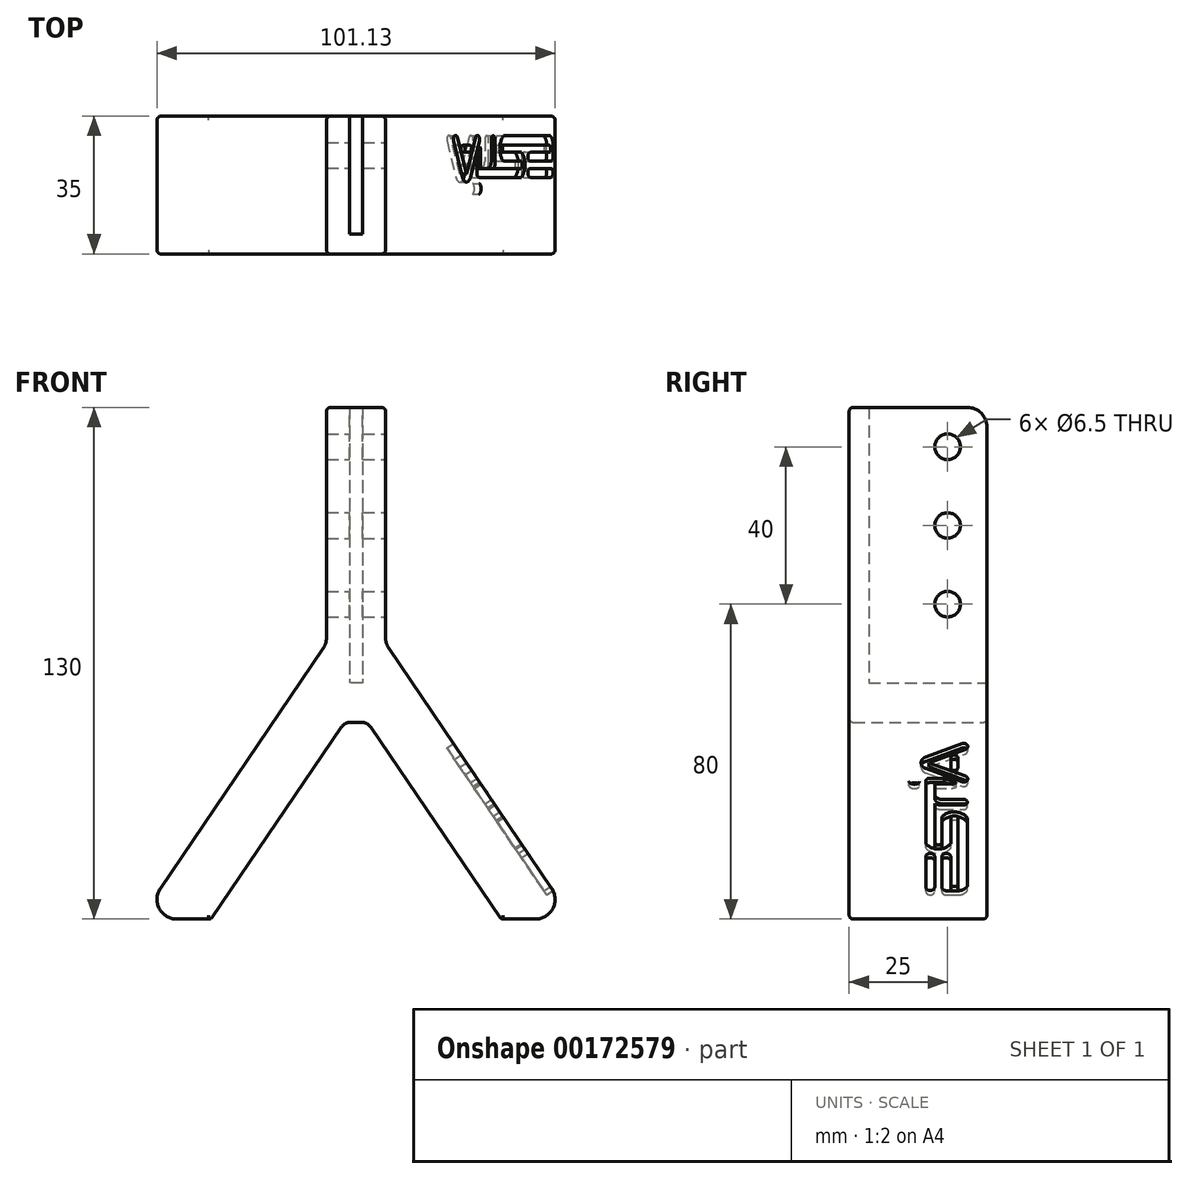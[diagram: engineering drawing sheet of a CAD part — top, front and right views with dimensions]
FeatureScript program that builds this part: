
annotation { "Feature Type Name" : "Feature", "Feature Type Description" : "" }
export const myFeature = defineFeature(function(context is Context, id is Id, definition is map)
    precondition{}
    {
        {
            var Q0;
            Q0=qCreatedBy(makeId("Front.planeOp"),FACE);
            var sketch = newSketch(context, id + "F0", { "sketchPlane" : qUnion([Q0])});
            skLineSegment(sketch, "E0", {"start": v(0, 0) * mm, "end": v(137.14, 0) * mm});
            skLineSegment(sketch, "E1", {"start": v(137.14, 0) * mm, "end": v(68.57, 101.05) * mm});
            skPoint(sketch, "E1.endSnap0", {"position": v(68.57, 0) * mm});
            skLineSegment(sketch, "E2", {"start": v(68.57, 101.05) * mm, "end": v(0, 0) * mm});
            skLineSegment(sketch, "E3.bottom", {"start": v(61.07, 90) * mm, "end": v(76.07, 90) * mm});
            skLineSegment(sketch, "E3.top", {"start": v(61.07, 150) * mm, "end": v(76.07, 150) * mm});
            skLineSegment(sketch, "E3.left", {"start": v(61.07, 90) * mm, "end": v(61.07, 150) * mm});
            skLineSegment(sketch, "E3.right", {"start": v(76.07, 90) * mm, "end": v(76.07, 150) * mm});
            skLineSegment(sketch, "E4.bottom", {"start": v(13.57, 0) * mm, "end": v(123.57, 0) * mm});
            skLineSegment(sketch, "E4.top", {"start": v(13.57, 20) * mm, "end": v(123.57, 20) * mm});
            skLineSegment(sketch, "E4.left", {"start": v(13.57, 0) * mm, "end": v(13.57, 20) * mm});
            skLineSegment(sketch, "E4.right", {"start": v(123.57, 0) * mm, "end": v(123.57, 20) * mm});
            skSolve(sketch);
        }
        {
            var Q0;
            Q0=makeQuery(id+"F0.imprint","IMPRINT",FACE,{"disambiguationData":[TD([[makeQuery(id+"F0.imprint","IMPRINT",EDGE,{"derivedFrom":sQuery(id+"F0.wireOp",EDGE,"E4.bottom")}),1.0]])]});
            var Q1;
            {var subQ0=sQuery(id+"F0.wireOp",EDGE,"E3.bottom");Q1=makeQuery(id+"F0.imprint","IMPRINT",FACE,{"disambiguationData":[TD([[makeQuery(id+"F0.imprint","IMPRINT",EDGE,{"derivedFrom":subQ0}),-1.0]])]});}
            var Q2;
            {var subQ3=sQuery(id+"F0.wireOp",EDGE,"E3.bottom");Q2=makeQuery(id+"F0.imprint","IMPRINT",FACE,{"disambiguationData":[TD([[makeQuery(id+"F0.imprint","IMPRINT",EDGE,{"derivedFrom":subQ3}),1.0]])]});}
            var Q3;
            Q3=makeQuery(id+"F0.imprint","IMPRINT",FACE,{"disambiguationData":[TD([[makeQuery(id+"F0.imprint","IMPRINT",EDGE,{"derivedFrom":sQuery(id+"F0.wireOp",EDGE,"E3.top")}),-1.0]])]});
            extrude(context, id + "F1", {"entities" : qUnion([Q0, Q1, Q2, Q3]), "depth" : 35 * mm, "offsetDistance" : 25 * mm});
        }
        {
            var Q0;
            Q0=makeQuery(id+"F1.opExtrude","CAP_FACE",FACE,{"disambiguationData":[OSD([sQuery(id+"F0.wireOp",EDGE,"E0"),sQuery(id+"F0.wireOp",EDGE,"E1"),sQuery(id+"F0.wireOp",EDGE,"E2"),sQuery(id+"F0.wireOp",EDGE,"E3.top"),sQuery(id+"F0.wireOp",EDGE,"E3.left"),sQuery(id+"F0.wireOp",EDGE,"E3.right")])],"isStart":true});
            var sketch = newSketch(context, id + "F2", { "sketchPlane" : qUnion([Q0])});
            skLineSegment(sketch, "E5.bottom", {"start": v(-70.27, 150) * mm, "end": v(-66.87, 150) * mm});
            skLineSegment(sketch, "E5.top", {"start": v(-70.27, 80) * mm, "end": v(-66.87, 80) * mm});
            skLineSegment(sketch, "E5.left", {"start": v(-70.27, 150) * mm, "end": v(-70.27, 80) * mm});
            skLineSegment(sketch, "E5.right", {"start": v(-66.87, 150) * mm, "end": v(-66.87, 80) * mm});
            skSolve(sketch);
        }
        {
            var Q0;
            Q0 = qSketchRegion(id + "F2", true);
            extrude(context, id + "F3", {"entities" : qUnion([Q0]), "operationType" : NewBodyOperationType.REMOVE, "oppositeDirection" : true, "depth" : 30 * mm, "offsetDistance" : 25 * mm});
        }
        {
            var Q0;
            Q0=makeQuery(id+"F1.opExtrude","SWEPT_FACE",FACE,{"disambiguationData":[OSD([sQuery(id+"F0.wireOp",EDGE,"E3.right")])]});
            var sketch = newSketch(context, id + "F4", { "sketchPlane" : qUnion([Q0])});
            skCircle(sketch, "E6", {"center": v(-10, 140) * mm, "radius": 3.25 * mm});
            skCircle(sketch, "E7", {"center": v(-10, 120) * mm, "radius": 3.25 * mm});
            skCircle(sketch, "E8", {"center": v(-10, 100) * mm, "radius": 3.25 * mm});
            skSolve(sketch);
        }
        {
            var Q0;
            Q0 = qSketchRegion(id + "F4", true);
            extrude(context, id + "F5", {"entities" : qUnion([Q0]), "operationType" : NewBodyOperationType.REMOVE, "oppositeDirection" : true, "depth" : 25 * mm, "offsetDistance" : 25 * mm});
        }
        {
            var Q0;
            Q0=makeQuery(id+"F1.opExtrude","CAP_FACE",FACE,{"disambiguationData":[OSD([sQuery(id+"F0.wireOp",EDGE,"E1"),sQuery(id+"F0.wireOp",EDGE,"E2"),sQuery(id+"F0.wireOp",EDGE,"E3.top"),sQuery(id+"F0.wireOp",EDGE,"E3.left"),sQuery(id+"F0.wireOp",EDGE,"E3.right"),sQuery(id+"F0.wireOp",EDGE,"E4.bottom"),sQuery(id+"F0.wireOp",EDGE,"E4.left"),sQuery(id+"F0.wireOp",EDGE,"E4.right")])],"isStart":true});
            var sketch = newSketch(context, id + "F6", { "sketchPlane" : qUnion([Q0])});
            skLineSegment(sketch, "E9", {"start": v(-112.23, 10) * mm, "end": v(-71.52, 70) * mm});
            skLineSegment(sketch, "E10", {"start": v(-71.52, 70) * mm, "end": v(-65.63, 70) * mm});
            skLineSegment(sketch, "E11", {"start": v(-65.63, 70) * mm, "end": v(-24.91, 10) * mm});
            skLineSegment(sketch, "E12", {"start": v(-24.91, 10) * mm, "end": v(-112.23, 10) * mm});
            skSolve(sketch);
        }
        {
            var Q0;
            Q0 = qSketchRegion(id + "F6", true);
            extrude(context, id + "F7", {"entities" : qUnion([Q0]), "operationType" : NewBodyOperationType.REMOVE, "endBound" : BoundingType.THROUGH_ALL, "oppositeDirection" : true, "depth" : 25 * mm, "offsetDistance" : 25 * mm});
        }
        {
            var Q0;
            Q0=makeQuery(id+"F7.boolean.opBoolean","COPY",EDGE,{"derivedFrom":makeQuery(id+"F7.opExtrude","SWEPT_EDGE",EDGE,{"disambiguationData":[OSD([sQuery(id+"F6.wireOp",EDGE,"E11"),sQuery(id+"F6.wireOp",EDGE,"E12")])]})});
            var Q1;
            Q1=makeQuery(id+"F7.boolean.opBoolean","COPY",EDGE,{"derivedFrom":makeQuery(id+"F7.opExtrude","SWEPT_EDGE",EDGE,{"disambiguationData":[OSD([sQuery(id+"F6.wireOp",EDGE,"E9"),sQuery(id+"F6.wireOp",EDGE,"E12")])]})});
            var Q2;
            Q2=makeQuery(id+"F1.opExtrude","SWEPT_EDGE",EDGE,{"disambiguationData":[OSD([sQuery(id+"F0.wireOp",EDGE,"E2"),sQuery(id+"F0.wireOp",EDGE,"E4.top"),sQuery(id+"F0.wireOp",EDGE,"E4.left")])]});
            var Q3;
            Q3=makeQuery(id+"F1.opExtrude","SWEPT_EDGE",EDGE,{"disambiguationData":[OSD([sQuery(id+"F0.wireOp",EDGE,"E1"),sQuery(id+"F0.wireOp",EDGE,"E4.top"),sQuery(id+"F0.wireOp",EDGE,"E4.right")])]});
            var Q4;
            Q4=makeQuery(id+"F1.opExtrude","SWEPT_EDGE",EDGE,{"disambiguationData":[OSD([sQuery(id+"F0.wireOp",EDGE,"E2"),sQuery(id+"F0.wireOp",EDGE,"E3.bottom"),sQuery(id+"F0.wireOp",EDGE,"E3.left")])]});
            var Q5;
            Q5=makeQuery(id+"F1.opExtrude","SWEPT_EDGE",EDGE,{"disambiguationData":[OSD([sQuery(id+"F0.wireOp",EDGE,"E1"),sQuery(id+"F0.wireOp",EDGE,"E3.bottom"),sQuery(id+"F0.wireOp",EDGE,"E3.right")])]});
            fillet(context, id + "F8", {"entities" : qUnion([Q0, Q1, Q2, Q3, Q4, Q5]), "radius" : 5 * mm, "tangentPropagation" : true, "allowEdgeOverflow" : false});
        }
        {
            var Q0;
            Q0=makeQuery(id+"F7.boolean.opBoolean","COPY",EDGE,{"derivedFrom":makeQuery(id+"F7.opExtrude","SWEPT_EDGE",EDGE,{"disambiguationData":[OSD([sQuery(id+"F6.wireOp",EDGE,"E9"),sQuery(id+"F6.wireOp",EDGE,"E10")])]})});
            var Q1;
            Q1=makeQuery(id+"F7.boolean.opBoolean","COPY",EDGE,{"derivedFrom":makeQuery(id+"F7.opExtrude","SWEPT_EDGE",EDGE,{"disambiguationData":[OSD([sQuery(id+"F6.wireOp",EDGE,"E10"),sQuery(id+"F6.wireOp",EDGE,"E11")])]})});
            fillet(context, id + "F9", {"entities" : qUnion([Q0, Q1]), "radius" : 3 * mm, "tangentPropagation" : true, "allowEdgeOverflow" : false});
        }
        {
            var Q0;
            {var subQ0=sQuery(id+"F0.wireOp",EDGE,"E3.right");var subQ1=sQuery(id+"F0.wireOp",EDGE,"E3.top");Q0=makeQuery(id+"F3.boolean.opBoolean","SPLIT",EDGE,{"disambiguationData":[TD([makeQuery(id+"F1.opExtrude","SWEPT_FACE",FACE,{"disambiguationData":[OSD([subQ0])]})])],"derivedFrom":makeQuery(id+"F1.opExtrude","CAP_EDGE",EDGE,{"disambiguationData":[OSD([subQ1])],"isStart":true})});}
            var Q1;
            {var subQ0=sQuery(id+"F0.wireOp",EDGE,"E3.left");var subQ1=sQuery(id+"F0.wireOp",EDGE,"E3.top");Q1=makeQuery(id+"F3.boolean.opBoolean","SPLIT",EDGE,{"disambiguationData":[TD([makeQuery(id+"F1.opExtrude","SWEPT_FACE",FACE,{"disambiguationData":[OSD([subQ0])]})])],"derivedFrom":makeQuery(id+"F1.opExtrude","CAP_EDGE",EDGE,{"disambiguationData":[OSD([subQ1])],"isStart":true})});}
            fillet(context, id + "F10", {"entities" : qUnion([Q0, Q1]), "radius" : 5 * mm, "tangentPropagation" : true, "allowEdgeOverflow" : false});
        }
        {
            var Q0;
            Q0=makeQuery(id+"F1.opExtrude","CAP_EDGE",EDGE,{"disambiguationData":[OSD([sQuery(id+"F0.wireOp",EDGE,"E3.right")])],"isStart":false});
            var Q1;
            Q1=makeQuery(id+"F1.opExtrude","CAP_EDGE",EDGE,{"disambiguationData":[OSD([sQuery(id+"F0.wireOp",EDGE,"E3.left")])],"isStart":false});
            fillet(context, id + "F11", {"entities" : qUnion([Q0, Q1]), "radius" : 1 * mm, "tangentPropagation" : true, "allowEdgeOverflow" : false});
        }
        {
            var Q0;
            Q0=makeQuery(id+"F1.opExtrude","CAP_EDGE",EDGE,{"disambiguationData":[OSD([sQuery(id+"F0.wireOp",EDGE,"E3.top")])],"isStart":false});
            fillet(context, id + "F12", {"entities" : qUnion([Q0]), "radius" : 1 * mm, "tangentPropagation" : true, "allowEdgeOverflow" : false});
        }
        {
            var Q0;
            Q0=makeQuery(id+"F7.boolean.opBoolean","COPY",EDGE,{"derivedFrom":makeQuery(id+"F7.opExtrude","CAP_EDGE",EDGE,{"disambiguationData":[OSD([sQuery(id+"F6.wireOp",EDGE,"E11")])],"isStart":true})});
            var Q1;
            Q1=makeQuery(id+"F7.boolean.opBoolean","INTERSECT",EDGE,{"derivedFrom":[makeQuery(id+"F1.opExtrude","CAP_FACE",FACE,{"disambiguationData":[OSD([sQuery(id+"F0.wireOp",EDGE,"E1"),sQuery(id+"F0.wireOp",EDGE,"E2"),sQuery(id+"F0.wireOp",EDGE,"E3.top"),sQuery(id+"F0.wireOp",EDGE,"E3.left"),sQuery(id+"F0.wireOp",EDGE,"E3.right"),sQuery(id+"F0.wireOp",EDGE,"E4.bottom"),sQuery(id+"F0.wireOp",EDGE,"E4.left"),sQuery(id+"F0.wireOp",EDGE,"E4.right")])],"isStart":false}),makeQuery(id+"F7.opExtrude","SWEPT_FACE",FACE,{"disambiguationData":[OSD([sQuery(id+"F6.wireOp",EDGE,"E11")])]})]});
            fillet(context, id + "F13", {"entities" : qUnion([Q0, Q1]), "radius" : 1 * mm, "tangentPropagation" : true, "allowEdgeOverflow" : false});
        }
        {
            var Q0;
            Q0=makeQuery(id+"F1.opExtrude","SWEPT_FACE",FACE,{"disambiguationData":[OSD([sQuery(id+"F0.wireOp",EDGE,"E1")])]});
            var sketch = newSketch(context, id + "F14", { "sketchPlane" : qUnion([Q0])});
            skLineSegment(sketch, "E13.0.0", {"start": v(-7.78, -42.77) * mm, "end": v(-9.2, -42.77) * mm});
            skLineSegment(sketch, "E13.0.1", {"start": v(-9.2, -42.77) * mm, "end": v(-9.2, -33.77) * mm});
            skLineSegment(sketch, "E13.0.38", {"start": v(-11.48, -33.77) * mm, "end": v(-11.48, -42.9) * mm});
            skLineSegment(sketch, "E13.0.57", {"start": v(-10.28, -44.1) * mm, "end": v(-7.34, -44.1) * mm});
            skArc(sketch, "E13.0.59", {"start": v(-7.34, -44.1) * mm, "mid": v(-6, -43.75) * mm, "end": v(-5, -42.77) * mm});
            skLineSegment(sketch, "E13.0.60", {"start": v(-5, -42.77) * mm, "end": v(-5, -21.7) * mm});
            skArc(sketch, "E13.0.61", {"start": v(-5, -21.7) * mm, "mid": v(-8.2, -19.91) * mm, "end": v(-11.48, -21.55) * mm});
            skLineSegment(sketch, "E13.0.62", {"start": v(-11.48, -21.55) * mm, "end": v(-11.48, -29.73) * mm});
            skArc(sketch, "E13.0.63", {"start": v(-11.48, -29.73) * mm, "mid": v(-12.38, -30.04) * mm, "end": v(-13.27, -29.7) * mm});
            skLineSegment(sketch, "E13.0.64", {"start": v(-13.27, -29.7) * mm, "end": v(-13.27, -17.32) * mm});
            skArc(sketch, "E13.0.65", {"start": v(-13.27, -17.32) * mm, "mid": v(-12.4, -17.7) * mm, "end": v(-11.46, -17.82) * mm});
            skLineSegment(sketch, "E13.0.66", {"start": v(-11.46, -17.82) * mm, "end": v(-5.86, -17.82) * mm});
            skArc(sketch, "E13.0.67", {"start": v(-5.86, -17.82) * mm, "mid": v(-5, -16.96) * mm, "end": v(-5.86, -16.1) * mm});
            skLineSegment(sketch, "E13.0.68", {"start": v(-5.86, -16.1) * mm, "end": v(-11.46, -16.1) * mm});
            skArc(sketch, "E13.0.69", {"start": v(-11.46, -16.1) * mm, "mid": v(-12.74, -15.56) * mm, "end": v(-13.27, -14.28) * mm});
            skLineSegment(sketch, "E13.0.70", {"start": v(-13.27, -14.28) * mm, "end": v(-13.27, -11.3) * mm});
            skLineSegment(sketch, "E13.0.71", {"start": v(-13.27, -11.3) * mm, "end": v(-9, -11.3) * mm});
            skArc(sketch, "E13.0.72", {"start": v(-9, -11.3) * mm, "mid": v(-8.36, -11.2) * mm, "end": v(-7.78, -10.89) * mm});
            skLineSegment(sketch, "E13.0.73", {"start": v(-7.78, -10.89) * mm, "end": v(-10.78, -9.58) * mm});
            skLineSegment(sketch, "E13.0.74", {"start": v(-10.78, -9.58) * mm, "end": v(-14.6, -9.58) * mm});
            skArc(sketch, "E13.0.75", {"start": v(-14.6, -9.58) * mm, "mid": v(-15.28, -9.86) * mm, "end": v(-15.55, -10.53) * mm});
            skLineSegment(sketch, "E13.0.76", {"start": v(-15.55, -10.53) * mm, "end": v(-15.55, -29.67) * mm});
            skArc(sketch, "E13.0.77", {"start": v(-15.55, -29.67) * mm, "mid": v(-12.39, -31.34) * mm, "end": v(-9.2, -29.73) * mm});
            skLineSegment(sketch, "E13.0.78", {"start": v(-9.2, -29.73) * mm, "end": v(-9.2, -21.55) * mm});
            skArc(sketch, "E13.0.79", {"start": v(-9.2, -21.55) * mm, "mid": v(-8.3, -21.12) * mm, "end": v(-7.4, -21.55) * mm});
            skLineSegment(sketch, "E13.0.80", {"start": v(-7.4, -21.55) * mm, "end": v(-7.4, -42.39) * mm});
            skArc(sketch, "E13.0.81", {"start": v(-7.4, -42.39) * mm, "mid": v(-7.5, -42.66) * mm, "end": v(-7.78, -42.77) * mm});
            skLineSegment(sketch, "E14.0.2", {"start": v(-13.27, -42.9) * mm, "end": v(-13.27, -33.77) * mm});
            skLineSegment(sketch, "E14.0.39", {"start": v(-15.55, -33.77) * mm, "end": v(-15.55, -42.9) * mm});
            skLineSegment(sketch, "E15.0.0", {"start": v(-14.77, -4.83) * mm, "end": v(-5.47, -0.77) * mm});
            skArc(sketch, "E15.0.1", {"start": v(-5.47, -0.77) * mm, "mid": v(-4.96, 0.52) * mm, "end": v(-6.25, 1.02) * mm});
            skLineSegment(sketch, "E15.0.2", {"start": v(-6.25, 1.02) * mm, "end": v(-15.55, -3.04) * mm});
            skArc(sketch, "E15.0.3", {"start": v(-15.55, -3.04) * mm, "mid": v(-16.72, -4.83) * mm, "end": v(-15.55, -6.62) * mm});
            skLineSegment(sketch, "E15.0.4", {"start": v(-15.55, -6.62) * mm, "end": v(-6.25, -10.69) * mm});
            skArc(sketch, "E15.0.5", {"start": v(-6.25, -10.69) * mm, "mid": v(-4.96, -10.18) * mm, "end": v(-5.47, -8.9) * mm});
            skLineSegment(sketch, "E15.0.6", {"start": v(-5.47, -8.9) * mm, "end": v(-14.77, -4.83) * mm});
            skLineSegment(sketch, "E16.0.2", {"start": v(-7.4, -6.33) * mm, "end": v(-7.4, -3.33) * mm});
            skLineSegment(sketch, "E16.0.39", {"start": v(-9.2, -3.33) * mm, "end": v(-9.2, -6.33) * mm});
            skLineSegment(sketch, "E17", {"start": v(-5.86, -16.96) * mm, "end": v(-5.86, 0.13) * mm, "construction": true});
            skLineSegment(sketch, "E18", {"start": v(-8.3, -22.26) * mm, "end": v(-8.3, -43.3) * mm, "construction": true});
            skLineSegment(sketch, "E19", {"start": v(-12.35, -47.78) * mm, "end": v(-12.35, -28.66) * mm, "construction": true});
            skArc(sketch, "E20", {"start": v(-15.55, -42.9) * mm, "mid": v(-14.41, -44.05) * mm, "end": v(-13.27, -42.9) * mm});
            skArc(sketch, "E21", {"start": v(-13.27, -33.77) * mm, "mid": v(-14.41, -32.63) * mm, "end": v(-15.55, -33.77) * mm});
            skArc(sketch, "E22", {"start": v(-9.2, -33.77) * mm, "mid": v(-10.33, -32.63) * mm, "end": v(-11.48, -33.77) * mm});
            skArc(sketch, "E23", {"start": v(-11.48, -42.9) * mm, "mid": v(-11.13, -43.76) * mm, "end": v(-10.28, -44.1) * mm});
            skArc(sketch, "E24", {"start": v(-7.4, -3.33) * mm, "mid": v(-8.3, -2.43) * mm, "end": v(-9.2, -3.33) * mm});
            skArc(sketch, "E25", {"start": v(-9.2, -6.33) * mm, "mid": v(-8.3, -7.23) * mm, "end": v(-7.4, -6.33) * mm});
            skLineSegment(sketch, "E26", {"start": v(-8.3, -6.33) * mm, "end": v(-8.3, -3.33) * mm, "construction": true});
            skLineSegment(sketch, "E27", {"start": v(-8.3, -4.83) * mm, "end": v(-27.7, -4.83) * mm, "construction": true});
            skEllipse(sketch, "E28", {"center": v(-18.45, -10.53) * mm, "majorRadius": 1.33 * mm, "minorRadius": 0.9 * mm, "majorAxis": v(-1, 0)});
            skLineSegment(sketch, "E29", {"start": v(-15.55, -10.53) * mm, "end": v(-27.58, -10.53) * mm, "construction": true});
            skSolve(sketch);
        }
        {
            var Q0;
            Q0 = qSketchRegion(id + "F14", true);
            extrude(context, id + "F15", {"entities" : qUnion([Q0]), "operationType" : NewBodyOperationType.REMOVE, "oppositeDirection" : true, "depth" : 2 * mm, "offsetDistance" : 25 * mm});
        }
    });
